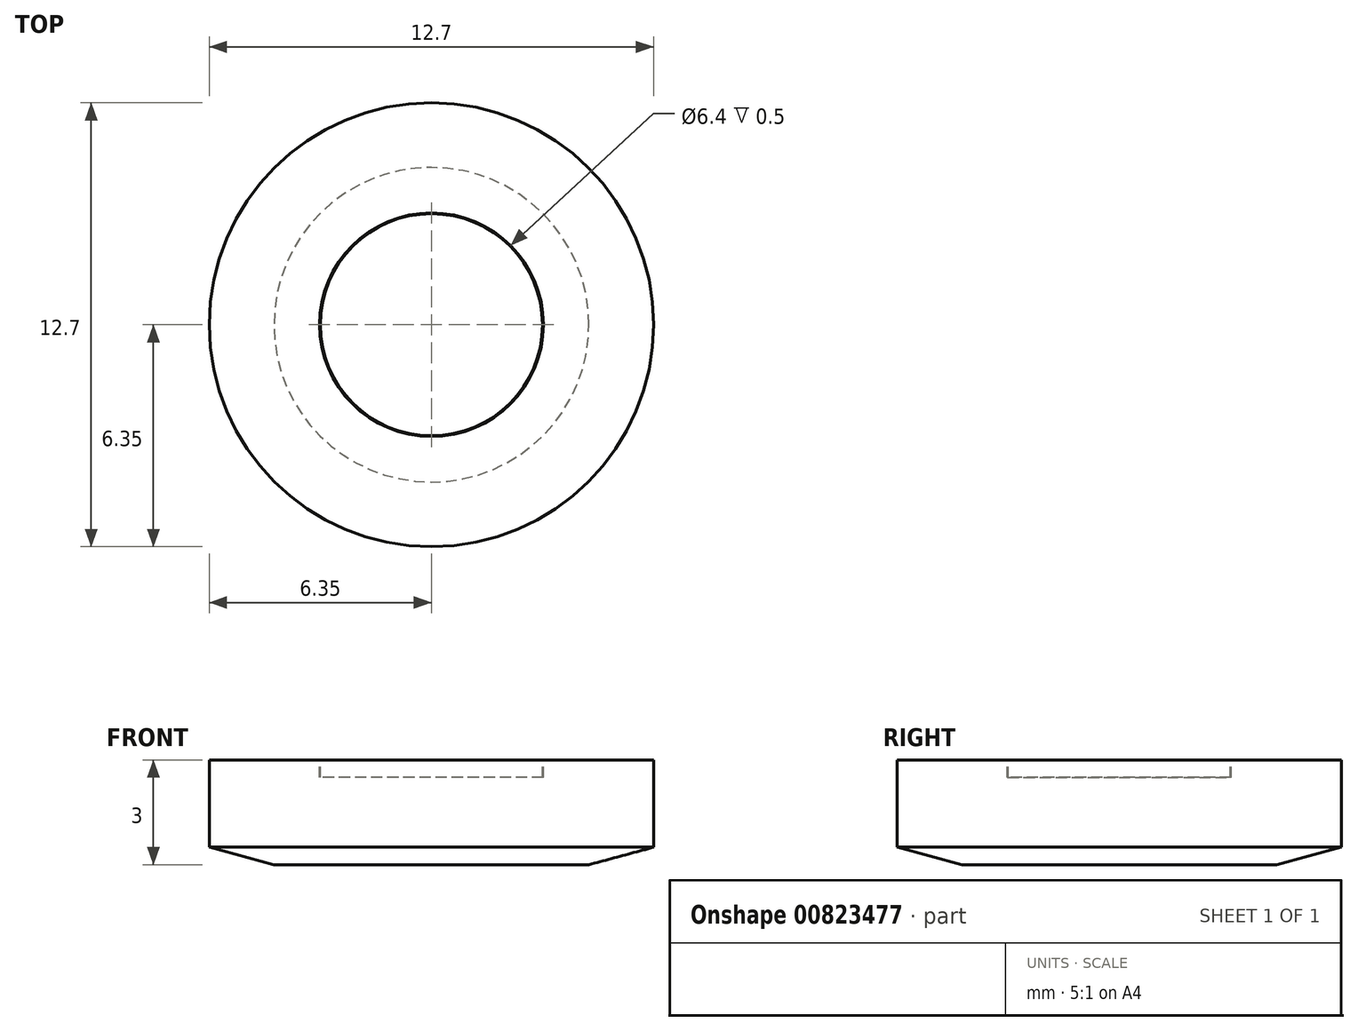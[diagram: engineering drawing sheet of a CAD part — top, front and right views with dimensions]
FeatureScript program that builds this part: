
annotation { "Feature Type Name" : "Feature", "Feature Type Description" : "" }
export const myFeature = defineFeature(function(context is Context, id is Id, definition is map)
    precondition{}
    {
        {
            var Q0;
            Q0=qCreatedBy(makeId("Top.planeOp"),FACE);
            var sketch = newSketch(context, id + "F0", { "sketchPlane" : qUnion([Q0])});
            skCircle(sketch, "E0", {"center": v(0, 0) * mm, "radius": 6.35 * mm});
            skSolve(sketch);
        }
        {
            var Q0;
            Q0=makeQuery(id+"F0.imprint","IMPRINT",FACE,{"disambiguationData":[TD([[makeQuery(id+"F0.imprint","IMPRINT",EDGE,{"derivedFrom":sQuery(id+"F0.wireOp",EDGE,"E0")}),1.0]])]});
            extrude(context, id + "F1", {"entities" : qUnion([Q0]), "depth" : 2.5 * mm, "offsetDistance" : 25 * mm});
        }
        {
            var Q0;
            Q0=makeQuery(id+"F1.opExtrude","CAP_FACE",FACE,{"disambiguationData":[OSD([sQuery(id+"F0.wireOp",EDGE,"E0")])],"isStart":false});
            var sketch = newSketch(context, id + "F2", { "sketchPlane" : qUnion([Q0])});
            skCircle(sketch, "E1", {"center": v(0, 0) * mm, "radius": 3.18 * mm});
            skCircle(sketch, "E2", {"center": v(0, 0) * mm, "radius": 3.2 * mm});
            skSolve(sketch);
        }
        {
            var Q0;
            Q0=makeQuery(id+"F2.imprint","IMPRINT",FACE,{"disambiguationData":[TD([[makeQuery(id+"F2.imprint","IMPRINT",EDGE,{"derivedFrom":sQuery(id+"F2.wireOp",EDGE,"E1")}),-1.0]])]});
            extrude(context, id + "F3", {"entities" : qUnion([Q0]), "operationType" : NewBodyOperationType.REMOVE, "oppositeDirection" : true, "depth" : .5 * mm, "offsetDistance" : 25 * mm});
        }
        {
            var Q0;
            Q0=qCreatedBy(makeId("Front.planeOp"),FACE);
            var sketch = newSketch(context, id + "F4", { "sketchPlane" : qUnion([Q0])});
            skLineSegment(sketch, "E3.0", {"start": v(-6.35, 0) * mm, "end": v(6.35, 0) * mm});
            skLineSegment(sketch, "E4", {"start": v(0, 0) * mm, "end": v(0, -0.5) * mm});
            skLineSegment(sketch, "E5", {"start": v(0, -0.5) * mm, "end": v(-4.5, -0.5) * mm});
            skLineSegment(sketch, "E6", {"start": v(-4.5, -0.5) * mm, "end": v(-6.35, 0) * mm});
            skSolve(sketch);
        }
        {
            var Q0;
            {var subQ2=sQuery(id+"F4.wireOp",EDGE,"E4");Q0=makeQuery(id+"F4.imprint","IMPRINT",FACE,{"disambiguationData":[TD([[makeQuery(id+"F4.imprint","IMPRINT",EDGE,{"derivedFrom":subQ2}),-1.0]])]});}
            var Q1;
            Q1=sQuery(id+"F4.wireOp",EDGE,"E4");
            revolve(context, id + "F5", {"operationType" : NewBodyOperationType.ADD, "surfaceOperationType" : NewSurfaceOperationType.NEW, "entities" : qUnion([Q0]), "axis" : qUnion([Q1]), "revolveType" : RevolveType.FULL});
        }
    });
